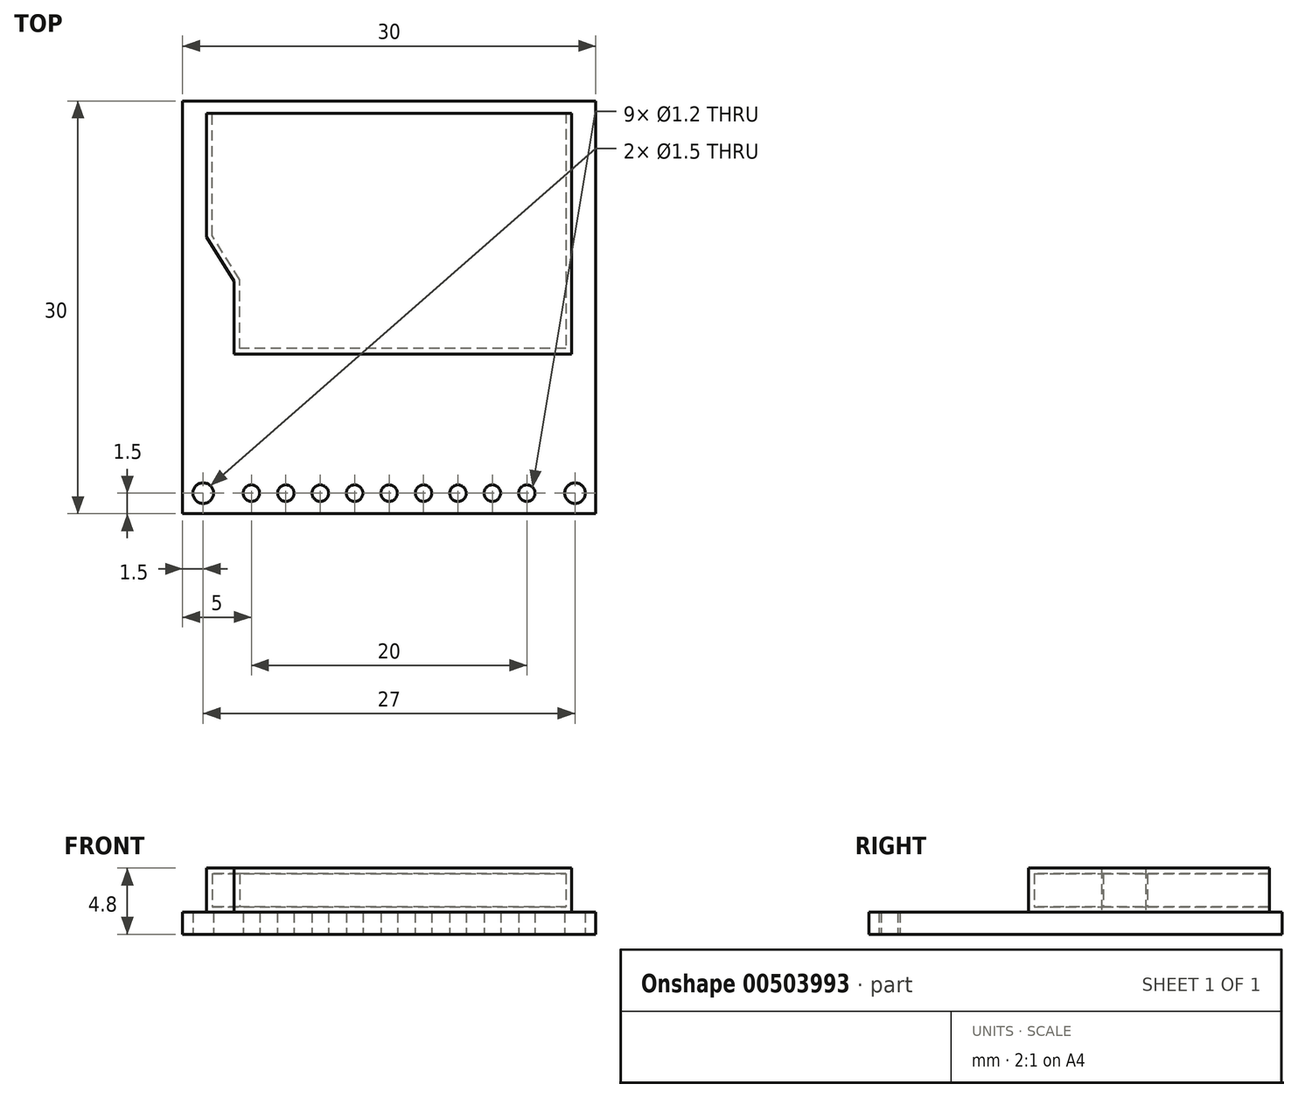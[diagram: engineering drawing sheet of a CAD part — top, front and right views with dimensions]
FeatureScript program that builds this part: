
annotation { "Feature Type Name" : "Feature", "Feature Type Description" : "" }
export const myFeature = defineFeature(function(context is Context, id is Id, definition is map)
    precondition{}
    {
        {
            var Q0;
            Q0=qCreatedBy(makeId("Top.planeOp"),FACE);
            var sketch = newSketch(context, id + "F0", { "sketchPlane" : qUnion([Q0])});
            skLineSegment(sketch, "E0.bottom", {"start": v(15, -15) * mm, "end": v(-15, -15) * mm});
            skLineSegment(sketch, "E0.top", {"start": v(15, 15) * mm, "end": v(-15, 15) * mm});
            skLineSegment(sketch, "E0.left", {"start": v(15, -15) * mm, "end": v(15, 15) * mm});
            skLineSegment(sketch, "E0.right", {"start": v(-15, -15) * mm, "end": v(-15, 15) * mm});
            skPoint(sketch, "E0.middle", {"position": v(0, 0) * mm});
            skCircle(sketch, "E1", {"center": v(-13.5, -13.5) * mm, "radius": 0.75 * mm});
            skLineSegment(sketch, "E2", {"start": v(0, -15) * mm, "end": v(0, 0) * mm, "construction": true});
            skCircle(sketch, "E3.MirrorC", {"center": v(13.5, -13.5) * mm, "radius": 0.75 * mm});
            skCircle(sketch, "E4", {"center": v(-10, -13.5) * mm, "radius": 0.6 * mm});
            skCircle(sketch, "E5.1.0.0", {"center": v(-7.5, -13.5) * mm, "radius": 0.6 * mm});
            skCircle(sketch, "E5.2.0.0", {"center": v(-5, -13.5) * mm, "radius": 0.6 * mm});
            skCircle(sketch, "E5.3.0.0", {"center": v(-2.5, -13.5) * mm, "radius": 0.6 * mm});
            skCircle(sketch, "E5.4.0.0", {"center": v(0, -13.5) * mm, "radius": 0.6 * mm});
            skCircle(sketch, "E5.5.0.0", {"center": v(2.5, -13.5) * mm, "radius": 0.6 * mm});
            skCircle(sketch, "E5.6.0.0", {"center": v(5, -13.5) * mm, "radius": 0.6 * mm});
            skCircle(sketch, "E5.7.0.0", {"center": v(7.5, -13.5) * mm, "radius": 0.6 * mm});
            skCircle(sketch, "E5.8.0.0", {"center": v(10, -13.5) * mm, "radius": 0.6 * mm});
            skLineSegment(sketch, "E5.direction1", {"start": v(-10, -13.5) * mm, "end": v(-7.5, -13.5) * mm, "construction": true});
            skSolve(sketch);
        }
        {
            var Q0;
            Q0=makeQuery(id+"F0.imprint","IMPRINT",FACE,{"disambiguationData":[TD([[makeQuery(id+"F0.imprint","IMPRINT",EDGE,{"derivedFrom":sQuery(id+"F0.wireOp",EDGE,"E0.bottom")}),-1.0]])]});
            extrude(context, id + "F1", {"entities" : qUnion([Q0]), "depth" : 1.6 * mm, "offsetDistance" : 25 * mm});
        }
        {
            var Q0;
            Q0=makeQuery(id+"F1.opExtrude","CAP_FACE",FACE,{"disambiguationData":[OSD([sQuery(id+"F0.wireOp",EDGE,"E0.bottom"),sQuery(id+"F0.wireOp",EDGE,"E0.top"),sQuery(id+"F0.wireOp",EDGE,"E0.left"),sQuery(id+"F0.wireOp",EDGE,"E0.right"),sQuery(id+"F0.wireOp",EDGE,"E1"),sQuery(id+"F0.wireOp",EDGE,"E3.MirrorC"),sQuery(id+"F0.wireOp",EDGE,"E4"),sQuery(id+"F0.wireOp",EDGE,"E5.1.0.0"),sQuery(id+"F0.wireOp",EDGE,"E5.2.0.0"),sQuery(id+"F0.wireOp",EDGE,"E5.3.0.0"),sQuery(id+"F0.wireOp",EDGE,"E5.4.0.0"),sQuery(id+"F0.wireOp",EDGE,"E5.5.0.0"),sQuery(id+"F0.wireOp",EDGE,"E5.6.0.0"),sQuery(id+"F0.wireOp",EDGE,"E5.7.0.0"),sQuery(id+"F0.wireOp",EDGE,"E5.8.0.0")])],"isStart":false});
            var sketch = newSketch(context, id + "F2", { "sketchPlane" : qUnion([Q0])});
            skLineSegment(sketch, "E6", {"start": v(-13.25, 14.1) * mm, "end": v(13.25, 14.1) * mm});
            skLineSegment(sketch, "E7", {"start": v(13.25, 14.1) * mm, "end": v(13.25, -3.4) * mm});
            skLineSegment(sketch, "E8", {"start": v(13.25, -3.4) * mm, "end": v(-11.25, -3.4) * mm});
            skLineSegment(sketch, "E9", {"start": v(-11.25, -3.4) * mm, "end": v(-11.25, 1.9) * mm});
            skLineSegment(sketch, "E10", {"start": v(-11.25, 1.9) * mm, "end": v(-13.25, 5.1) * mm});
            skLineSegment(sketch, "E11", {"start": v(-13.25, 5.1) * mm, "end": v(-13.25, 14.1) * mm});
            skLineSegment(sketch, "E12", {"start": v(0, 0) * mm, "end": v(0, 15) * mm, "construction": true});
            skSolve(sketch);
        }
        {
            var Q0;
            Q0=makeQuery(id+"F2.imprint","IMPRINT",FACE,{"disambiguationData":[TD([[makeQuery(id+"F2.imprint","IMPRINT",EDGE,{"derivedFrom":sQuery(id+"F2.wireOp",EDGE,"E6")}),-1.0]])]});
            extrude(context, id + "F3", {"entities" : qUnion([Q0]), "depth" : 3.2 * mm, "offsetDistance" : 25 * mm});
        }
        {
            var Q0;
            Q0=makeQuery(id+"F3.opExtrude","SWEPT_FACE",FACE,{"disambiguationData":[OSD([sQuery(id+"F2.wireOp",EDGE,"E6")])]});
            shell(context, id + "F4", {"entities" : qUnion([Q0]), "thickness" : 0.4 * mm});
        }
    });
